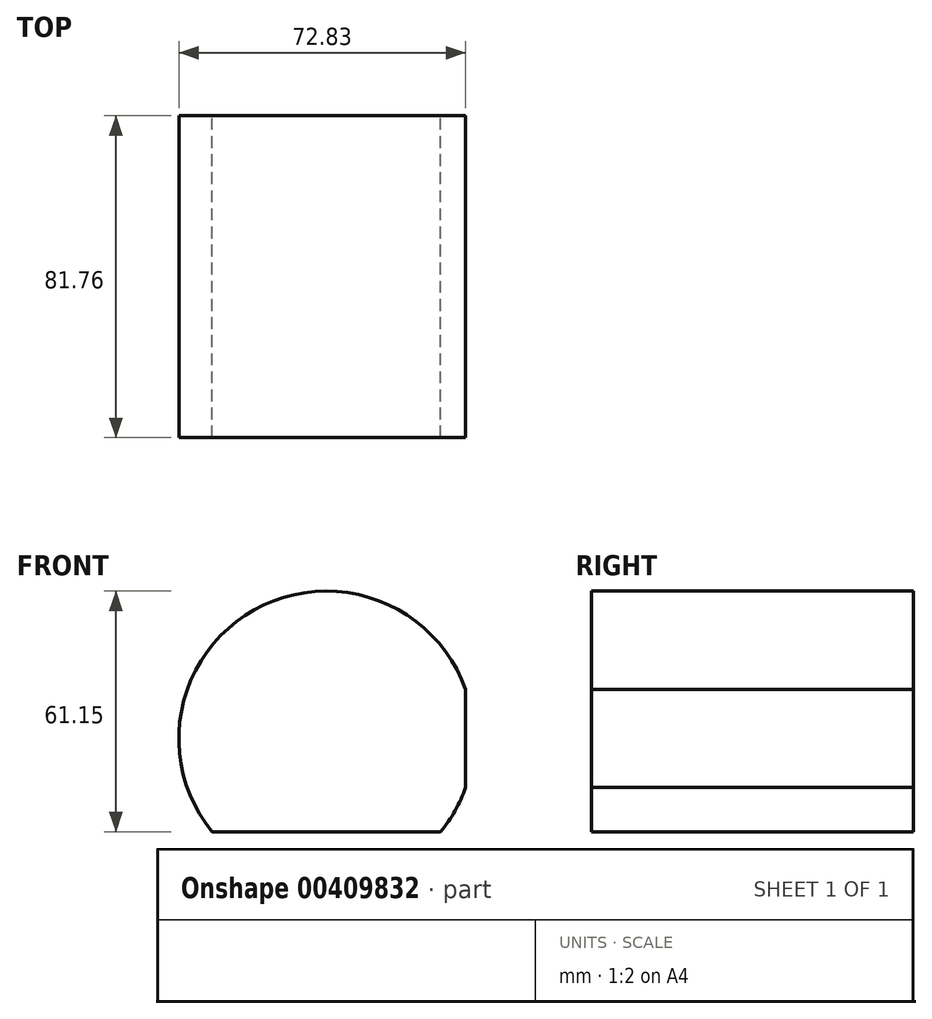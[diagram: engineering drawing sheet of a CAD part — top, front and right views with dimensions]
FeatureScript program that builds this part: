
annotation { "Feature Type Name" : "Feature", "Feature Type Description" : "" }
export const myFeature = defineFeature(function(context is Context, id is Id, definition is map)
    precondition{}
    {
        {
            var Q0;
            Q0=qCreatedBy(makeId("Front.planeOp"),FACE);
            var sketch = newSketch(context, id + "F0", { "sketchPlane" : qUnion([Q0])});
            skCircle(sketch, "E0", {"center": v(36.36, 23.67) * mm, "radius": 37.48 * mm});
            skPoint(sketch, "E0.first.point", {"position": v(0, 14.6) * mm});
            skPoint(sketch, "E0.second.point", {"position": v(0, 32.74) * mm});
            skPoint(sketch, "E0.third.point", {"position": v(65.42, 0) * mm});
            skCircle(sketch, "E1", {"center": v(-76.1, 124.44) * mm, "radius": 101.01 * mm});
            skPoint(sketch, "E1.first.point", {"position": v(-30.8, 214.72) * mm});
            skPoint(sketch, "E1.second.point", {"position": v(22, 148.55) * mm});
            skPoint(sketch, "E1.third.point", {"position": v(22.67, 103.26) * mm});
            skSolve(sketch);
        }
        {
            var Q0;
            Q0=makeQuery(id+"F0.imprint","IMPRINT",FACE,{"disambiguationData":[TD([[makeQuery(id+"F0.imprint","IMPRINT",EDGE,{"derivedFrom":sQuery(id+"F0.wireOp",EDGE,"E0")}),1.0]])]});
            extrude(context, id + "F1", {"entities" : qUnion([Q0]), "depth" : 196 * mm});
        }
        {
            var Q0;
            Q0=qCreatedBy(makeId("Top.planeOp"),FACE);
            var sketch = newSketch(context, id + "F2", { "sketchPlane" : qUnion([Q0])});
            skLineSegment(sketch, "E2.bottom", {"start": v(-37.46, -149.2) * mm, "end": v(71.72, -149.2) * mm});
            skLineSegment(sketch, "E2.top", {"start": v(-37.46, -67.45) * mm, "end": v(71.72, -67.45) * mm});
            skLineSegment(sketch, "E2.left", {"start": v(-37.46, -149.2) * mm, "end": v(-37.46, -67.45) * mm});
            skLineSegment(sketch, "E2.right", {"start": v(71.72, -149.2) * mm, "end": v(71.72, -67.45) * mm});
            skSolve(sketch);
        }
        {
            var Q0;
            Q0=makeQuery(id+"F2.imprint","IMPRINT",FACE,{"disambiguationData":[TD([[makeQuery(id+"F2.imprint","IMPRINT",EDGE,{"derivedFrom":sQuery(id+"F2.wireOp",EDGE,"E2.bottom")}),1.0]])]});
            var Q1;
            Q1 = qSketchRegion(id + "F2", true);
            extrude(context, id + "F3", {"entities" : qUnion([Q0, Q1]), "depth" : 113.56 * mm});
        }
        {
            var Q0;
            Q0=makeQuery(id+"F3.opExtrude","SWEPT_BODY",BODY,{"disambiguationData":[OSD([sQuery(id+"F2.wireOp",EDGE,"E2.bottom"),sQuery(id+"F2.wireOp",EDGE,"E2.top"),sQuery(id+"F2.wireOp",EDGE,"E2.left"),sQuery(id+"F2.wireOp",EDGE,"E2.right")])]});
            var Q1;
            Q1=makeQuery(id+"F1.opExtrude","SWEPT_BODY",BODY,{"disambiguationData":[OSD([sQuery(id+"F0.wireOp",EDGE,"E0")])]});
            booleanBodies(context, id + "F4", {"operationType" : BooleanOperationType.INTERSECTION, "tools" : qUnion([Q0, Q1])});
        }
    });
